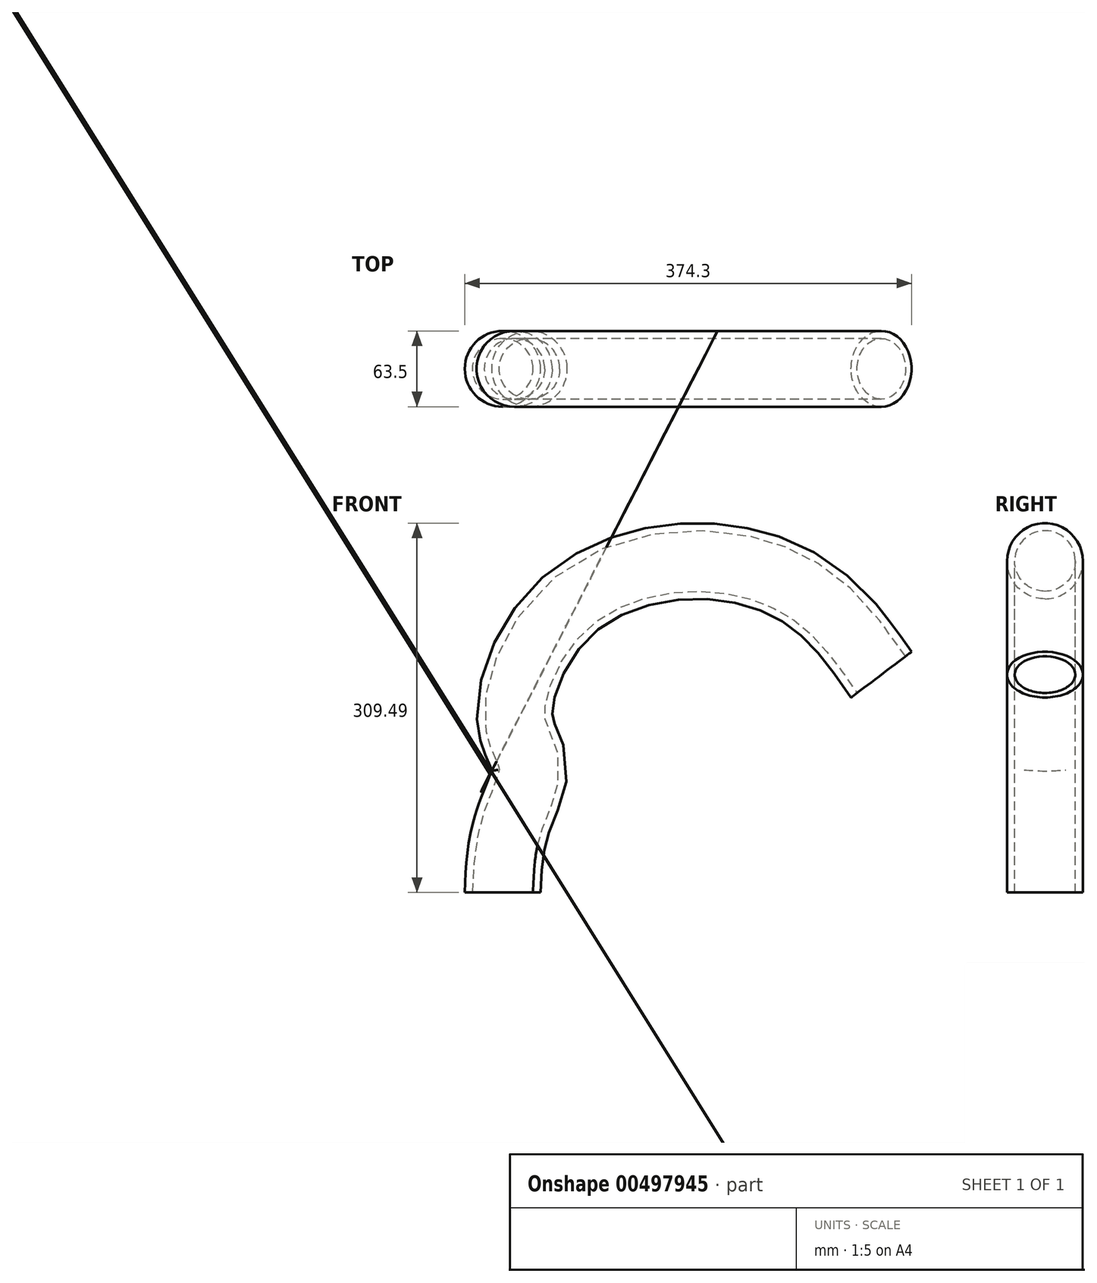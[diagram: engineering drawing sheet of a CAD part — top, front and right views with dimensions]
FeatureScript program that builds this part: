
annotation { "Feature Type Name" : "Feature", "Feature Type Description" : "" }
export const myFeature = defineFeature(function(context is Context, id is Id, definition is map)
    precondition{}
    {
        {
            var Q0;
            Q0=qCreatedBy(makeId("Top.planeOp"),FACE);
            var sketch = newSketch(context, id + "F0", { "sketchPlane" : qUnion([Q0])});
            skCircle(sketch, "E0", {"center": v(0, 0) * mm, "radius": 25.4 * mm});
            skCircle(sketch, "E1", {"center": v(0, 0) * mm, "radius": 31.75 * mm});
            skSolve(sketch);
        }
        {
            var Q0;
            Q0=qCreatedBy(makeId("Front.planeOp"),FACE);
            var sketch = newSketch(context, id + "F1", { "sketchPlane" : qUnion([Q0])});
            skFitSpline(sketch, "E2", {"points": [v(0, 0) * mm, v(7.32, 56.15) * mm, v(22.32, 105.52) * mm, v(10.22, 143.76) * mm, v(51.52, 237.5) * mm, v(165.84, 277.73) * mm, v(260.37, 247.71) * mm, v(317.21, 182.56) * mm], "startDerivative": vector(17.75, 460.15) * mm, "endDerivative": vector(330.13, -474.32) * mm});
            skSolve(sketch);
        }
        {
            var Q0;
            Q0=makeQuery(id+"F0.imprint","IMPRINT",FACE,{"disambiguationData":[TD([[makeQuery(id+"F0.imprint","IMPRINT",EDGE,{"derivedFrom":sQuery(id+"F0.wireOp",EDGE,"E0")}),-1.0]])]});
            var Q1;
            Q1=sQuery(id+"F1.wireOp",EDGE,"E2");
            sweep(context, id + "F2", {"profiles" : qUnion([Q0]), "path" : qUnion([Q1])});
        }
    });
